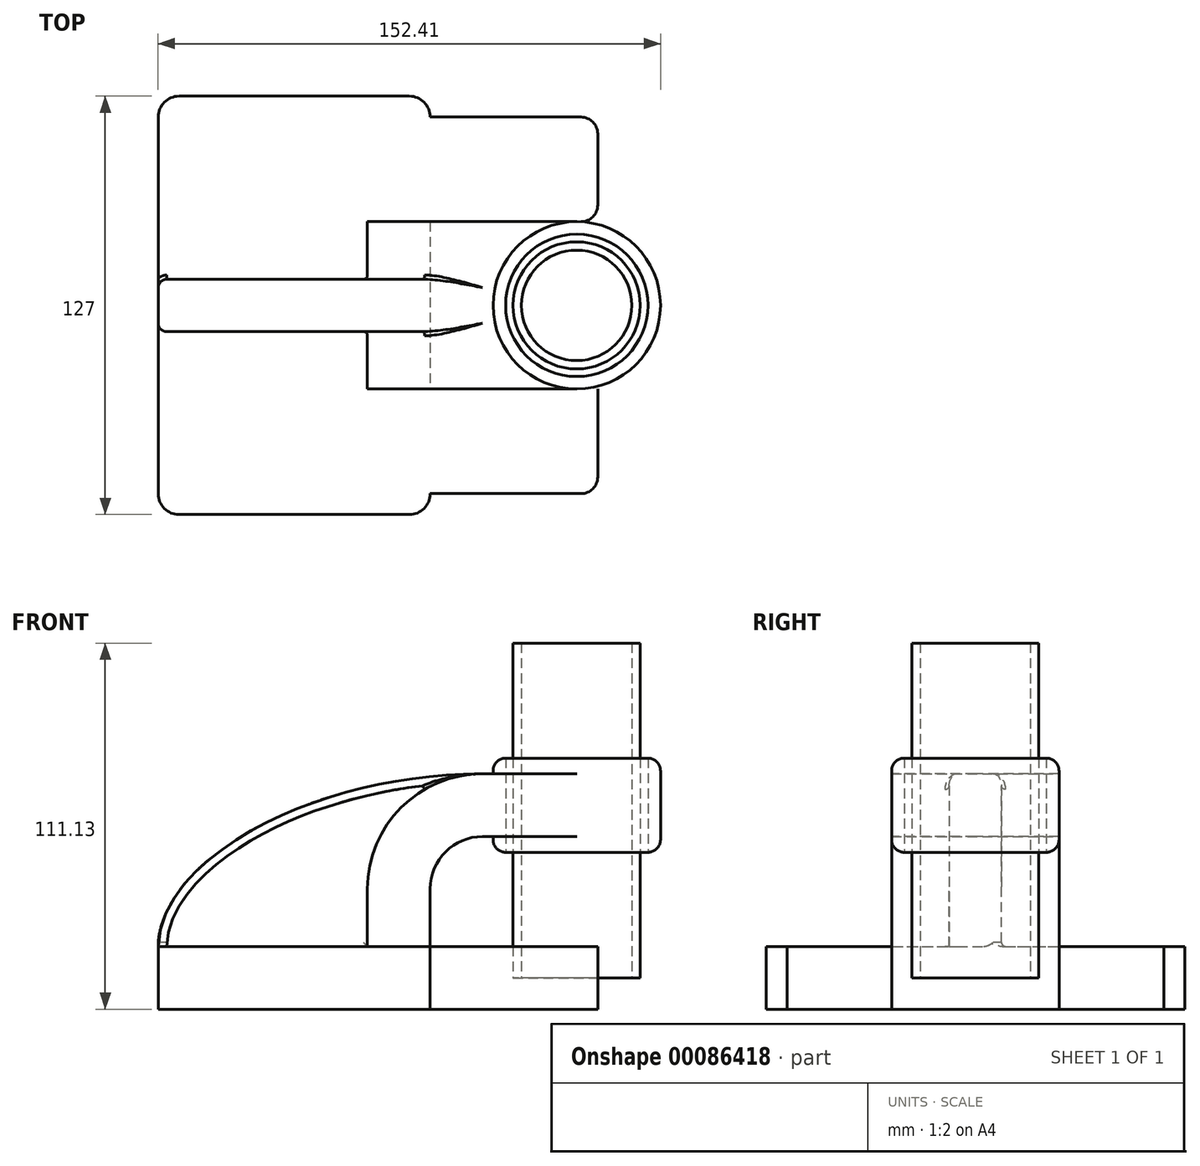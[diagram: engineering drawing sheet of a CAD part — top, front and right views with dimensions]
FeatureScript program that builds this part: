
annotation { "Feature Type Name" : "Feature", "Feature Type Description" : "" }
export const myFeature = defineFeature(function(context is Context, id is Id, definition is map)
    precondition{}
    {
        {
            var Q0;
            Q0=qCreatedBy(makeId("Front.planeOp"),FACE);
            var sketch = newSketch(context, id + "F0", { "sketchPlane" : qUnion([Q0])});
            skLineSegment(sketch, "E0.bottom", {"start": v(41.28, -9.52) * mm, "end": v(-41.28, -9.53) * mm});
            skLineSegment(sketch, "E0.top", {"start": v(41.28, 9.53) * mm, "end": v(-41.28, 9.53) * mm});
            skLineSegment(sketch, "E0.left", {"start": v(41.28, -9.52) * mm, "end": v(41.28, 9.53) * mm});
            skLineSegment(sketch, "E0.right", {"start": v(-41.28, -9.53) * mm, "end": v(-41.28, 9.53) * mm});
            skPoint(sketch, "E0.middle", {"position": v(0, 0) * mm});
            skLineSegment(sketch, "E1.bottom", {"start": v(111.13, 38.1) * mm, "end": v(60.33, 38.1) * mm});
            skLineSegment(sketch, "E1.top", {"start": v(111.13, 66.68) * mm, "end": v(60.33, 66.68) * mm});
            skLineSegment(sketch, "E1.left", {"start": v(111.13, 38.1) * mm, "end": v(111.13, 66.68) * mm});
            skLineSegment(sketch, "E1.right", {"start": v(60.33, 38.1) * mm, "end": v(60.33, 66.68) * mm});
            skPoint(sketch, "E1.middle", {"position": v(85.73, 52.39) * mm});
            skLineSegment(sketch, "E2", {"start": v(41.28, 9.53) * mm, "end": v(41.28, 27) * mm});
            skArc(sketch, "E3", {"start": v(41.27, 27) * mm, "mid": v(45.92, 38.23) * mm, "end": v(57.15, 42.88) * mm});
            skLineSegment(sketch, "E4", {"start": v(57.15, 42.88) * mm, "end": v(85.73, 42.88) * mm});
            skLineSegment(sketch, "E5.0", {"start": v(57.15, 61.93) * mm, "end": v(85.73, 61.93) * mm});
            skArc(sketch, "E5.1", {"start": v(22.23, 27) * mm, "mid": v(32.45, 51.7) * mm, "end": v(57.15, 61.93) * mm});
            skLineSegment(sketch, "E5.2", {"start": v(22.22, 9.53) * mm, "end": v(22.22, 27) * mm});
            skFitSpline(sketch, "E6", {"points": [v(-41.28, 9.52) * mm, v(57.15, 61.93) * mm], "startDerivative": vector(1.38, 79.5) * mm, "endDerivative": vector(154.6, 0.12) * mm});
            skLineSegment(sketch, "E7", {"start": v(85.73, 66.68) * mm, "end": v(85.73, 38.1) * mm});
            skLineSegment(sketch, "E8", {"start": v(85.73, 66.68) * mm, "end": v(85.73, 104.89) * mm});
            skLineSegment(sketch, "E9", {"start": v(85.73, 104.89) * mm, "end": v(85.73, 10.07) * mm});
            skSolve(sketch);
        }
        {
            var Q0;
            Q0=makeQuery(id+"F0.imprint","IMPRINT",FACE,{"disambiguationData":[TD([[makeQuery(id+"F0.imprint","IMPRINT",EDGE,{"derivedFrom":sQuery(id+"F0.wireOp",EDGE,"E0.bottom")}),-1.0]])]});
            extrude(context, id + "F1", {"entities" : qUnion([Q0]), "endBound" : BoundingType.SYMMETRIC, "depth" : 127 * mm});
        }
        {
            var Q0;
            {var subQ1=sQuery(id+"F0.wireOp",EDGE,"E2");Q0=makeQuery(id+"F0.imprint","IMPRINT",FACE,{"disambiguationData":[TD([[makeQuery(id+"F0.imprint","IMPRINT",EDGE,{"derivedFrom":subQ1}),1.0]])]});}
            var Q1;
            {var subQ0=sQuery(id+"F0.wireOp",EDGE,"PdMnpmZG-rQf2-gKya-Prxc-KW28ErSZuJgG");Q1=makeQuery(id+"F0.imprint","IMPRINT",FACE,{"disambiguationData":[TD([[makeQuery(id+"F0.imprint","IMPRINT",EDGE,{"derivedFrom":subQ0}),-1.0]])]});}
            var Q2;
            {var subQ0=sQuery(id+"F0.wireOp",EDGE,"E4");var subQ1=sQuery(id+"F0.wireOp",EDGE,"E1.right");var subQ2=makeQuery(id+"F0.imprint","INTERSECT",VERTEX,{"derivedFrom":[subQ1,subQ0]});Q2=makeQuery(id+"F0.imprint","IMPRINT",FACE,{"disambiguationData":[TD([[makeQuery(id+"F0.imprint","IMPRINT",EDGE,{"disambiguationData":[TD([[subQ2,-1.0]])],"derivedFrom":subQ1}),-1.0]])]});}
            extrude(context, id + "F2", {"entities" : qUnion([Q0, Q1, Q2]), "operationType" : NewBodyOperationType.ADD, "endBound" : BoundingType.SYMMETRIC, "depth" : 50.8 * mm});
        }
        {
            var Q0;
            {var subQ3=sQuery(id+"F0.wireOp",EDGE,"E5.2");Q0=makeQuery(id+"F0.imprint","IMPRINT",FACE,{"disambiguationData":[TD([[makeQuery(id+"F0.imprint","IMPRINT",EDGE,{"derivedFrom":subQ3}),1.0]])]});}
            extrude(context, id + "F3", {"entities" : qUnion([Q0]), "operationType" : NewBodyOperationType.ADD, "endBound" : BoundingType.SYMMETRIC, "depth" : 15.88 * mm});
        }
        {
            var Q0;
            {var subQ4=sQuery(id+"F0.wireOp",EDGE,"E1.left");Q0=makeQuery(id+"F0.imprint","IMPRINT",FACE,{"disambiguationData":[TD([[makeQuery(id+"F0.imprint","IMPRINT",EDGE,{"derivedFrom":subQ4}),1.0]])]});}
            var Q1;
            Q1=sQuery(id+"F0.wireOp",EDGE,"E7");
            revolve(context, id + "F4", {"operationType" : NewBodyOperationType.ADD, "entities" : qUnion([Q0]), "axis" : qUnion([Q1]), "revolveType" : RevolveType.FULL});
        }
        {
            var Q0;
            Q0=makeQuery(id+"F1.opExtrude","CAP_EDGE",EDGE,{"disambiguationData":[OSD([sQuery(id+"F0.wireOp",EDGE,"E0.right")])],"isStart":true});
            var Q1;
            Q1=makeQuery(id+"F1.opExtrude","CAP_EDGE",EDGE,{"disambiguationData":[OSD([sQuery(id+"F0.wireOp",EDGE,"E0.right")])],"isStart":false});
            var Q2;
            Q2=makeQuery(id+"F1.opExtrude","CAP_EDGE",EDGE,{"disambiguationData":[OSD([sQuery(id+"F0.wireOp",EDGE,"E0.left")])],"isStart":false});
            var Q3;
            Q3=makeQuery(id+"F1.opExtrude","CAP_EDGE",EDGE,{"disambiguationData":[OSD([sQuery(id+"F0.wireOp",EDGE,"E0.left")])],"isStart":true});
            fillet(context, id + "F5", {"entities" : qUnion([Q0, Q1, Q2, Q3]), "radius" : 6.35 * mm, "tangentPropagation" : true, "allowEdgeOverflow" : false});
        }
        {
            var Q0;
            Q0=makeQuery(id+"F3.opExtrude","CAP_EDGE",EDGE,{"disambiguationData":[OSD([sQuery(id+"F0.wireOp",EDGE,"E6")])],"isStart":false});
            var Q1;
            Q1=makeQuery(id+"F3.opExtrude","CAP_EDGE",EDGE,{"disambiguationData":[OSD([sQuery(id+"F0.wireOp",EDGE,"E6")])],"isStart":true});
            fillet(context, id + "F6", {"entities" : qUnion([Q0, Q1]), "radius" : 2.54 * mm, "tangentPropagation" : true, "allowEdgeOverflow" : false});
        }
        {
            var Q0;
            Q0=makeQuery(id+"F4.opRevolve","SWEPT_EDGE",EDGE,{"disambiguationData":[OSD([sQuery(id+"F0.wireOp",EDGE,"E1.top"),sQuery(id+"F0.wireOp",EDGE,"E1.left")])]});
            var Q1;
            Q1=makeQuery(id+"F4.opRevolve","SWEPT_EDGE",EDGE,{"disambiguationData":[OSD([sQuery(id+"F0.wireOp",EDGE,"E1.bottom"),sQuery(id+"F0.wireOp",EDGE,"E1.left")])]});
            fillet(context, id + "F7", {"entities" : qUnion([Q0, Q1]), "radius" : 3.8 * mm, "tangentPropagation" : true, "allowEdgeOverflow" : false});
        }
        {
            var Q0;
            Q0=makeQuery(id+"F4.opRevolve","SWEPT_FACE",FACE,{"disambiguationData":[OSD([sQuery(id+"F0.wireOp",EDGE,"E1.top")])]});
            extrude(context, id + "F8", {"entities" : qUnion([Q0]), "operationType" : NewBodyOperationType.REMOVE, "endBound" : BoundingType.SYMMETRIC, "depth" : 76.2 * mm});
        }
        {
            var Q0;
            Q0=makeQuery(id+"F2.boolean.opBoolean","MERGE",FACE,{"derivedFrom":[makeQuery(id+"F1.opExtrude","SWEPT_FACE",FACE,{"disambiguationData":[OSD([sQuery(id+"F0.wireOp",EDGE,"E0.left")])]}),makeQuery(id+"F2.opExtrude","SWEPT_FACE",FACE,{"disambiguationData":[OSD([sQuery(id+"F0.wireOp",EDGE,"E2")])]})]});
            extrude(context, id + "F9", {"entities" : qUnion([Q0]), "operationType" : NewBodyOperationType.ADD, "depth" : 50.8 * mm});
        }
        {
            var Q0;
            Q0=makeQuery(id+"F9.opExtrude","SWEPT_FACE",FACE,{"disambiguationData":[OSD([sQuery(id+"F0.wireOp",EDGE,"E2"),sQuery(id+"F0.wireOp",EDGE,"E3")])]});
            extrude(context, id + "F10", {"entities" : qUnion([Q0]), "operationType" : NewBodyOperationType.REMOVE, "oppositeDirection" : true, "depth" : 50.8 * mm});
        }
        {
            var Q0;
            {var subQ0=sQuery(id+"F0.wireOp",EDGE,"E2");var subQ1=sQuery(id+"F0.wireOp",EDGE,"E0.left");Q0=makeQuery(id+"F9.opExtrude","CAP_EDGE",EDGE,{"disambiguationData":[OSD([subQ1,subQ0]),TDD([makeQuery(id+"F5.opFillet","BLEND_EDGE",EDGE,{"blendedFrom":[makeQuery(id+"F1.opExtrude","CAP_EDGE",EDGE,{"disambiguationData":[OSD([subQ1])],"isStart":false}),makeQuery(id+"F2.boolean.opBoolean","MERGE",FACE,{"derivedFrom":[makeQuery(id+"F1.opExtrude","SWEPT_FACE",FACE,{"disambiguationData":[OSD([subQ1])]}),makeQuery(id+"F2.opExtrude","SWEPT_FACE",FACE,{"disambiguationData":[OSD([subQ0])]})]})],"blendedInto":[makeQuery(id+"F2.boolean.opBoolean","MERGE",FACE,{"derivedFrom":[makeQuery(id+"F1.opExtrude","SWEPT_FACE",FACE,{"disambiguationData":[OSD([subQ1])]}),makeQuery(id+"F2.opExtrude","SWEPT_FACE",FACE,{"disambiguationData":[OSD([subQ0])]})]})]})])],"isStart":false});}
            var Q1;
            {var subQ0=sQuery(id+"F0.wireOp",EDGE,"E3");var subQ1=sQuery(id+"F0.wireOp",EDGE,"E2");Q1=makeQuery(id+"F10.boolean.opBoolean","COPY",EDGE,{"derivedFrom":makeQuery(id+"F10.opExtrude","SWEPT_EDGE",EDGE,{"disambiguationData":[OSD([subQ1,subQ0]),TDD([makeQuery(id+"F9.opExtrude","CAP_VERTEX",VERTEX,{"disambiguationData":[OSD([subQ1,subQ0]),TDD([makeQuery(id+"F2.opExtrude","CAP_VERTEX",VERTEX,{"disambiguationData":[OSD([subQ1,subQ0])],"isStart":false})])],"isStart":false})])]})});}
            var Q2;
            {var subQ0=sQuery(id+"F0.wireOp",EDGE,"E3");var subQ1=sQuery(id+"F0.wireOp",EDGE,"E2");Q2=makeQuery(id+"F10.boolean.opBoolean","COPY",EDGE,{"derivedFrom":makeQuery(id+"F10.opExtrude","SWEPT_EDGE",EDGE,{"disambiguationData":[OSD([subQ1,subQ0]),TDD([makeQuery(id+"F9.opExtrude","CAP_VERTEX",VERTEX,{"disambiguationData":[OSD([subQ1,subQ0]),TDD([makeQuery(id+"F2.opExtrude","CAP_VERTEX",VERTEX,{"disambiguationData":[OSD([subQ1,subQ0])],"isStart":true})])],"isStart":false})])]})});}
            var Q3;
            {var subQ0=sQuery(id+"F0.wireOp",EDGE,"E2");var subQ1=sQuery(id+"F0.wireOp",EDGE,"E0.left");Q3=makeQuery(id+"F9.opExtrude","CAP_EDGE",EDGE,{"disambiguationData":[OSD([subQ1,subQ0]),TDD([makeQuery(id+"F5.opFillet","BLEND_EDGE",EDGE,{"blendedFrom":[makeQuery(id+"F1.opExtrude","CAP_EDGE",EDGE,{"disambiguationData":[OSD([subQ1])],"isStart":true}),makeQuery(id+"F2.boolean.opBoolean","MERGE",FACE,{"derivedFrom":[makeQuery(id+"F1.opExtrude","SWEPT_FACE",FACE,{"disambiguationData":[OSD([subQ1])]}),makeQuery(id+"F2.opExtrude","SWEPT_FACE",FACE,{"disambiguationData":[OSD([subQ0])]})]})],"blendedInto":[makeQuery(id+"F2.boolean.opBoolean","MERGE",FACE,{"derivedFrom":[makeQuery(id+"F1.opExtrude","SWEPT_FACE",FACE,{"disambiguationData":[OSD([subQ1])]}),makeQuery(id+"F2.opExtrude","SWEPT_FACE",FACE,{"disambiguationData":[OSD([subQ0])]})]})]})])],"isStart":false});}
            fillet(context, id + "F11", {"entities" : qUnion([Q0, Q1, Q2, Q3]), "radius" : 5.08 * mm, "tangentPropagation" : true, "allowEdgeOverflow" : false});
        }
        {
            var Q0;
            Q0=qCreatedBy(makeId("Top.planeOp"),FACE);
            var sketch = newSketch(context, id + "F12", { "sketchPlane" : qUnion([Q0])});
            skCircle(sketch, "E10", {"center": v(85.68, 0) * mm, "radius": 19.3 * mm});
            skSolve(sketch);
        }
        {
            var Q0;
            Q0=makeQuery(id+"F12.imprint","IMPRINT",FACE,{"disambiguationData":[TD([[makeQuery(id+"F12.imprint","IMPRINT",EDGE,{"derivedFrom":sQuery(id+"F12.wireOp",EDGE,"E10")}),1.0]])]});
            extrude(context, id + "F13", {"entities" : qUnion([Q0]), "depth" : 101.6 * mm});
        }
        {
            var Q0;
            Q0=makeQuery(id+"F13.opExtrude","CAP_FACE",FACE,{"disambiguationData":[OSD([sQuery(id+"F12.wireOp",EDGE,"E10")])],"isStart":false});
            var Q1;
            Q1=makeQuery(id+"F13.opExtrude","CAP_FACE",FACE,{"disambiguationData":[OSD([sQuery(id+"F12.wireOp",EDGE,"E10")])],"isStart":true});
            shell(context, id + "F14", {"entities" : qUnion([Q0, Q1]), "thickness" : 2.54 * mm});
        }
        {
            var Q0;
            Q0=makeQuery(id+"F3.opExtrude","CAP_EDGE",EDGE,{"disambiguationData":[OSD([sQuery(id+"F0.wireOp",EDGE,"E0.top")])],"isStart":false});
            var Q1;
            Q1=makeQuery(id+"F3.opExtrude","CAP_EDGE",EDGE,{"disambiguationData":[OSD([sQuery(id+"F0.wireOp",EDGE,"E0.top")])],"isStart":true});
            var Q2;
            {var subQ0=sQuery(id+"F0.wireOp",EDGE,"E0.top");var subQ1=sQuery(id+"F0.wireOp",EDGE,"E6");var subQ2=sQuery(id+"F0.wireOp",EDGE,"E5.2");var subQ3=sQuery(id+"F0.wireOp",EDGE,"E5.1");Q2=makeQuery(id+"F3.boolean.opBoolean","SPLIT",EDGE,{"disambiguationData":[TD([makeQuery(id+"F3.opExtrude","CAP_FACE",FACE,{"disambiguationData":[OSD([subQ0,subQ3,subQ2,subQ1])],"isStart":true})])],"derivedFrom":makeQuery(id+"F2.opExtrude","SWEPT_EDGE",EDGE,{"disambiguationData":[OSD([subQ0,subQ2])]})});}
            var Q3;
            {var subQ0=sQuery(id+"F0.wireOp",EDGE,"E0.top");var subQ1=sQuery(id+"F0.wireOp",EDGE,"E6");var subQ2=sQuery(id+"F0.wireOp",EDGE,"E5.2");var subQ3=sQuery(id+"F0.wireOp",EDGE,"E5.1");Q3=makeQuery(id+"F3.boolean.opBoolean","SPLIT",EDGE,{"disambiguationData":[TD([makeQuery(id+"F3.opExtrude","CAP_FACE",FACE,{"disambiguationData":[OSD([subQ0,subQ3,subQ2,subQ1])],"isStart":false})])],"derivedFrom":makeQuery(id+"F2.opExtrude","SWEPT_EDGE",EDGE,{"disambiguationData":[OSD([subQ0,subQ2])]})});}
            var Q4;
            Q4=makeQuery(id+"F3.opExtrude","CAP_EDGE",EDGE,{"disambiguationData":[OSD([sQuery(id+"F0.wireOp",EDGE,"E5.1")])],"isStart":false});
            var Q5;
            Q5=makeQuery(id+"F3.opExtrude","CAP_EDGE",EDGE,{"disambiguationData":[OSD([sQuery(id+"F0.wireOp",EDGE,"E5.2")])],"isStart":false});
            var Q6;
            Q6=makeQuery(id+"F3.opExtrude","CAP_EDGE",EDGE,{"disambiguationData":[OSD([sQuery(id+"F0.wireOp",EDGE,"E5.2")])],"isStart":true});
            var Q7;
            Q7=makeQuery(id+"F3.opExtrude","CAP_EDGE",EDGE,{"disambiguationData":[OSD([sQuery(id+"F0.wireOp",EDGE,"E5.1")])],"isStart":true});
            var Q8;
            {var subQ0=sQuery(id+"F0.wireOp",EDGE,"E6");var subQ1=sQuery(id+"F0.wireOp",EDGE,"E5.2");var subQ2=sQuery(id+"F0.wireOp",EDGE,"E5.1");var subQ3=sQuery(id+"F0.wireOp",EDGE,"E0.top");Q8=makeQuery(id+"F6.opFillet","BLEND_EDGE",EDGE,{"blendedFrom":[makeQuery(id+"F3.opExtrude","CAP_EDGE",EDGE,{"disambiguationData":[OSD([subQ0])],"isStart":true}),makeQuery(id+"F3.boolean.opBoolean","SPLIT",FACE,{"disambiguationData":[TD([makeQuery(id+"F3.opExtrude","CAP_FACE",FACE,{"disambiguationData":[OSD([subQ3,subQ2,subQ1,subQ0])],"isStart":true})])],"derivedFrom":makeQuery(id+"F2.opExtrude","SWEPT_FACE",FACE,{"disambiguationData":[OSD([subQ2])]})})],"blendedInto":[makeQuery(id+"F3.boolean.opBoolean","SPLIT",FACE,{"disambiguationData":[TD([makeQuery(id+"F3.opExtrude","CAP_FACE",FACE,{"disambiguationData":[OSD([subQ3,subQ2,subQ1,subQ0])],"isStart":true})])],"derivedFrom":makeQuery(id+"F2.opExtrude","SWEPT_FACE",FACE,{"disambiguationData":[OSD([subQ2])]})})]});}
            var Q9;
            {var subQ0=sQuery(id+"F0.wireOp",EDGE,"E6");var subQ1=sQuery(id+"F0.wireOp",EDGE,"E5.2");var subQ2=sQuery(id+"F0.wireOp",EDGE,"E5.1");var subQ3=sQuery(id+"F0.wireOp",EDGE,"E0.top");Q9=makeQuery(id+"F6.opFillet","BLEND_EDGE",EDGE,{"blendedFrom":[makeQuery(id+"F3.opExtrude","CAP_EDGE",EDGE,{"disambiguationData":[OSD([subQ0])],"isStart":false}),makeQuery(id+"F3.boolean.opBoolean","SPLIT",FACE,{"disambiguationData":[TD([makeQuery(id+"F3.opExtrude","CAP_FACE",FACE,{"disambiguationData":[OSD([subQ3,subQ2,subQ1,subQ0])],"isStart":false})])],"derivedFrom":makeQuery(id+"F2.opExtrude","SWEPT_FACE",FACE,{"disambiguationData":[OSD([subQ2])]})})],"blendedInto":[makeQuery(id+"F3.boolean.opBoolean","SPLIT",FACE,{"disambiguationData":[TD([makeQuery(id+"F3.opExtrude","CAP_FACE",FACE,{"disambiguationData":[OSD([subQ3,subQ2,subQ1,subQ0])],"isStart":false})])],"derivedFrom":makeQuery(id+"F2.opExtrude","SWEPT_FACE",FACE,{"disambiguationData":[OSD([subQ2])]})})]});}
            fillet(context, id + "F15", {"entities" : qUnion([Q0, Q1, Q2, Q3, Q4, Q5, Q6, Q7, Q8, Q9]), "radius" : 1.27 * mm, "tangentPropagation" : true, "allowEdgeOverflow" : false});
        }
    });
